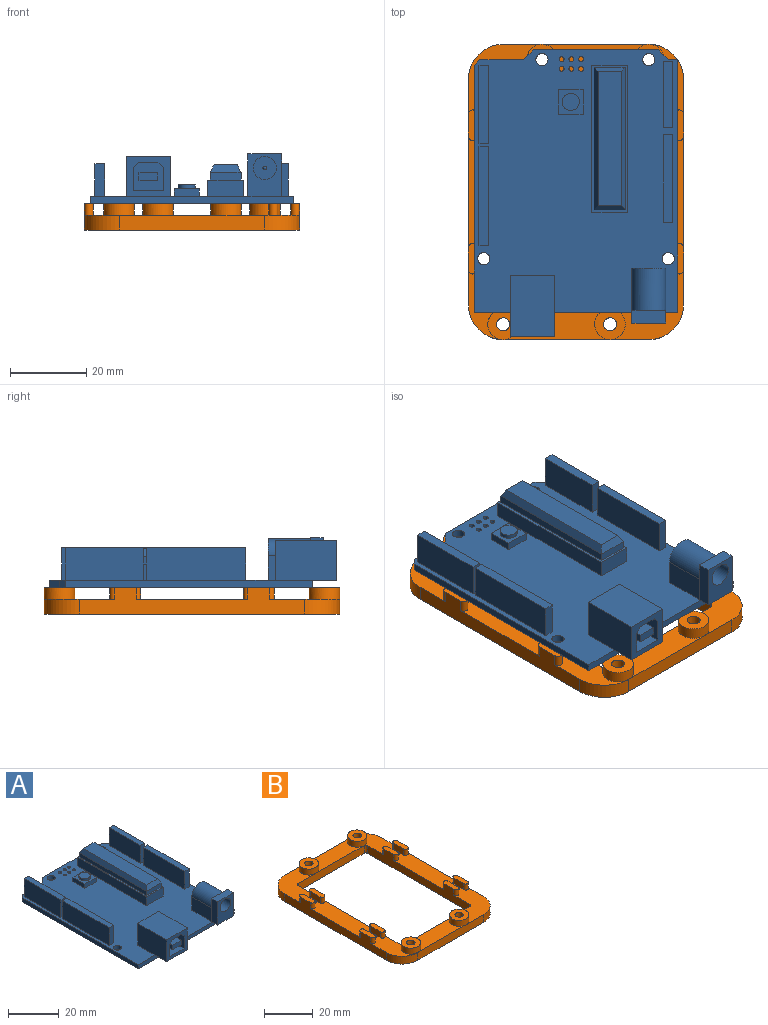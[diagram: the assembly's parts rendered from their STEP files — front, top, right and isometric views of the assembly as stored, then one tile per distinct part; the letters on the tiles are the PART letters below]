
ASSEMBLY  parts=2 mates=1
PART A: 159 faces, bbox 53.3x75x13 mm
  f0: plane 68.58x53.34mm, normal (0,0,1), area 2744.3mm2, adj f1,f2,f3,f4,f5,f6,f7,f8
  f1: plane 2.54x2.54mm, normal (0.71,0.71,0), area 6.8mm2, adj f0,f2,f51,f52
  f2: plane 32.77x1.9mm, normal (0,1,0), area 62.3mm2, adj f0,f1,f3,f52
  f3: plane 2.54x2.54mm, normal (-0.71,0.71,0), area 6.8mm2, adj f0,f2,f4,f52
  f4: plane 11.43x1.9mm, normal (0,1,0), area 21.7mm2, adj f0,f3,f5,f52
  f5: plane 1.9x1.52mm, normal (-0.71,0.71,0), area 4.1mm2, adj f0,f4,f6,f52
  f6: plane 64.52x1.9mm, normal (-1,0,0), area 122.6mm2, adj f0,f5,f7,f52
  f7: plane 53.34x1.9mm, normal (0,-1,0), area 101.3mm2, adj f0,f6,f8,f52,f81,f99,f107,f108
  f8: plane 66.04x1.9mm, normal (1,0,0), area 125.5mm2, adj f0,f7,f51,f52
  f9: cylinder r=1.59mm len=3.18mm, axis (0,0,-1), area 19mm2, adj f0,f52
  f10: cylinder r=1.59mm len=3.18mm, axis (0,0,-1), area 19mm2, adj f0,f52
  f11: cylinder r=1.59mm len=3.18mm, axis (0,0,-1), area 19mm2, adj f0,f52
  f12: cylinder r=1.59mm len=3.18mm, axis (0,0,-1), area 19mm2, adj f0,f52
  f13: cylinder r=0.64mm len=1.9mm, axis (0,0,-1), area 7.6mm2, adj f52,f80
  f14: cylinder r=0.64mm len=1.9mm, axis (0,0,-1), area 7.6mm2, adj f52,f79
  f15: cylinder r=0.64mm len=1.9mm, axis (0,0,-1), area 7.6mm2, adj f52,f78
  f16: cylinder r=0.64mm len=1.9mm, axis (0,0,-1), area 7.6mm2, adj f52,f77
  f17: cylinder r=0.64mm len=1.9mm, axis (0,0,-1), area 7.6mm2, adj f52,f76
  f18: cylinder r=0.64mm len=1.9mm, axis (0,0,-1), area 7.6mm2, adj f52,f75
  f19: cylinder r=0.64mm len=1.9mm, axis (0,0,-1), area 7.6mm2, adj f52,f74
  f20: cylinder r=0.64mm len=1.9mm, axis (0,0,-1), area 7.6mm2, adj f52,f73
  f21: cylinder r=0.64mm len=1.9mm, axis (0,0,-1), area 7.6mm2, adj f52,f72
  f22: cylinder r=0.64mm len=1.9mm, axis (0,0,-1), area 7.6mm2, adj f52,f71
  f23: cylinder r=0.64mm len=1.9mm, axis (0,0,-1), area 7.6mm2, adj f52,f58
  f24: cylinder r=0.64mm len=1.9mm, axis (0,0,-1), area 7.6mm2, adj f52,f140
  f25: cylinder r=0.64mm len=1.9mm, axis (0,0,-1), area 7.6mm2, adj f52,f151
  f26: cylinder r=0.64mm len=1.9mm, axis (0,0,-1), area 7.6mm2, adj f52,f59
  f27: cylinder r=0.64mm len=1.9mm, axis (0,0,-1), area 7.6mm2, adj f52,f60
  f28: cylinder r=0.64mm len=1.9mm, axis (0,0,-1), area 7.6mm2, adj f52,f61
  f29: cylinder r=0.64mm len=1.9mm, axis (0,0,-1), area 7.6mm2, adj f52,f62
  f30: cylinder r=0.64mm len=1.9mm, axis (0,0,-1), area 7.6mm2, adj f52,f63
  f31: cylinder r=0.64mm len=1.9mm, axis (0,0,-1), area 7.6mm2, adj f52,f64
  f32: cylinder r=0.64mm len=1.9mm, axis (0,0,-1), area 7.6mm2, adj f52,f65
  f33: cylinder r=0.64mm len=1.9mm, axis (0,0,-1), area 7.6mm2, adj f52,f139
  f34: cylinder r=0.64mm len=1.9mm, axis (0,0,-1), area 7.6mm2, adj f52,f138
  f35: cylinder r=0.64mm len=1.9mm, axis (0,0,-1), area 7.6mm2, adj f52,f137
  f36: cylinder r=0.64mm len=1.9mm, axis (0,0,-1), area 7.6mm2, adj f52,f136
  f37: cylinder r=0.64mm len=1.9mm, axis (0,0,-1), area 7.6mm2, adj f52,f135
  f38: cylinder r=0.64mm len=1.9mm, axis (0,0,-1), area 7.6mm2, adj f52,f134
  f39: cylinder r=0.64mm len=1.9mm, axis (0,0,-1), area 7.6mm2, adj f52,f133
  f40: cylinder r=0.64mm len=1.9mm, axis (0,0,-1), area 7.6mm2, adj f52,f150
  f41: cylinder r=0.64mm len=1.9mm, axis (0,0,-1), area 7.6mm2, adj f52,f149
  f42: cylinder r=0.64mm len=1.9mm, axis (0,0,-1), area 7.6mm2, adj f52,f148
  f43: cylinder r=0.64mm len=1.9mm, axis (0,0,-1), area 7.6mm2, adj f52,f147
  f44: cylinder r=0.64mm len=1.9mm, axis (0,0,-1), area 7.6mm2, adj f52,f146
  f45: cylinder r=0.64mm len=1.9mm, axis (0,0,-1), area 7.6mm2, adj f0,f52
  f46: cylinder r=0.64mm len=1.9mm, axis (0,0,-1), area 7.6mm2, adj f0,f52
  f47: cylinder r=0.64mm len=1.9mm, axis (0,0,-1), area 7.6mm2, adj f0,f52
  f48: cylinder r=0.64mm len=1.9mm, axis (0,0,-1), area 7.6mm2, adj f0,f52
  f49: cylinder r=0.64mm len=1.9mm, axis (0,0,-1), area 7.6mm2, adj f0,f52
  f50: cylinder r=0.64mm len=1.9mm, axis (0,0,-1), area 7.6mm2, adj f0,f52
  f51: plane 2.54x1.9mm, normal (0,1,0), area 4.8mm2, adj f0,f1,f8,f52
  f52: plane 68.58x53.34mm, normal (0,0,-1), area 3531.3mm2, adj f1,f2,f3,f4,f5,f6,f7,f8
  f53: plane 20.48x2.5mm, normal (0,0,1), area 51.2mm2, adj f54,f55,f56,f57
  f54: plane 8.6x2.5mm, normal (0,1,0), area 21.5mm2, adj f0,f53,f55,f57
  f55: plane 20.48x8.6mm, normal (1,0,0), area 176.1mm2, adj f0,f53,f54,f56
  f56: plane 8.6x2.5mm, normal (0,-1,0), area 21.5mm2, adj f0,f53,f55,f57
  f57: plane 20.48x8.6mm, normal (-1,0,0), area 176.1mm2, adj f0,f53,f54,f56
  f58: plane 1.27x1.27mm, normal (0,0,-1), area 1.3mm2, adj f23
  f59: plane 1.27x1.27mm, normal (0,0,-1), area 1.3mm2, adj f26
  f60: plane 1.27x1.27mm, normal (0,0,-1), area 1.3mm2, adj f27
  f61: plane 1.27x1.27mm, normal (0,0,-1), area 1.3mm2, adj f28
  f62: plane 1.27x1.27mm, normal (0,0,-1), area 1.3mm2, adj f29
  f63: plane 1.27x1.27mm, normal (0,0,-1), area 1.3mm2, adj f30
  f64: plane 1.27x1.27mm, normal (0,0,-1), area 1.3mm2, adj f31
  f65: plane 1.27x1.27mm, normal (0,0,-1), area 1.3mm2, adj f32
  f66: plane 26x2.5mm, normal (0,0,1), area 65mm2, adj f67,f68,f69,f70
  f67: plane 26x8.6mm, normal (1,0,0), area 223.6mm2, adj f0,f66,f68,f70
  f68: plane 8.6x2.5mm, normal (0,-1,0), area 21.5mm2, adj f0,f66,f67,f69
  f69: plane 26x8.6mm, normal (-1,0,0), area 223.6mm2, adj f0,f66,f68,f70
  f70: plane 8.6x2.5mm, normal (0,1,0), area 21.5mm2, adj f0,f66,f67,f69
  f71: plane 1.27x1.27mm, normal (0,0,-1), area 1.3mm2, adj f22
  f72: plane 1.27x1.27mm, normal (0,0,-1), area 1.3mm2, adj f21
  f73: plane 1.27x1.27mm, normal (0,0,-1), area 1.3mm2, adj f20
  f74: plane 1.27x1.27mm, normal (0,0,-1), area 1.3mm2, adj f19
  f75: plane 1.27x1.27mm, normal (0,0,-1), area 1.3mm2, adj f18
  f76: plane 1.27x1.27mm, normal (0,0,-1), area 1.3mm2, adj f17
  f77: plane 1.27x1.27mm, normal (0,0,-1), area 1.3mm2, adj f16
  f78: plane 1.27x1.27mm, normal (0,0,-1), area 1.3mm2, adj f15
  f79: plane 1.27x1.27mm, normal (0,0,-1), area 1.3mm2, adj f14
  f80: plane 1.27x1.27mm, normal (0,0,-1), area 1.3mm2, adj f13
  f81: plane 11.6x6.38mm, normal (0,0,-1), area 73.9mm2, adj f7,f82,f83,f85
  f82: plane 11.6x10.5mm, normal (0,-1,0), area 64.6mm2, adj f81,f83,f85,f86,f87,f88,f89,f90
  f83: plane 16x10.5mm, normal (1,0,0), area 168mm2, adj f0,f81,f82,f84,f86
  f84: plane 11.6x10.5mm, normal (0,1,0), area 121.8mm2, adj f0,f83,f85,f86
  f85: plane 16x10.5mm, normal (-1,0,0), area 168mm2, adj f0,f81,f82,f84,f86
  f86: plane 16x11.6mm, normal (0,0,1), area 185.6mm2, adj f82,f83,f84,f85
  f87: plane 14.14x5.02mm, normal (0,0,-1), area 71mm2, adj f82,f88,f92,f93
  f88: plane 14.14x1.44mm, normal (0.71,0,-0.71), area 28.8mm2, adj f82,f87,f89,f93
  f89: plane 14.14x6.06mm, normal (1,0,0), area 85.7mm2, adj f82,f88,f90,f93
  f90: plane 14.14x7.9mm, normal (0,0,1), area 111.7mm2, adj f82,f89,f91,f93
  f91: plane 14.14x6.06mm, normal (-1,0,0), area 85.7mm2, adj f82,f90,f92,f93
  f92: plane 14.14x1.44mm, normal (-0.71,0,-0.71), area 28.8mm2, adj f82,f87,f91,f93
  f93: plane 7.9x7.5mm, normal (0,-1,0), area 47mm2, adj f87,f88,f89,f90,f91,f92,f95,f96
  f94: plane 4.88x2.08mm, normal (0,-1,0), area 10.2mm2, adj f95,f96,f97,f98
  f95: plane 14.14x4.88mm, normal (0,0,1), area 69mm2, adj f93,f94,f96,f98
  f96: plane 14.14x2.08mm, normal (-1,0,0), area 29.4mm2, adj f93,f94,f95,f97
  f97: plane 14.14x4.88mm, normal (0,0,-1), area 69mm2, adj f93,f94,f96,f98
  f98: plane 14.14x2.08mm, normal (1,0,0), area 29.4mm2, adj f93,f94,f95,f97
  f99: plane 8.88x2.88mm, normal (0,0,-1), area 25.5mm2, adj f7,f107,f108,f109
  f100: plane 11x6.49mm, normal (1,0,0), area 71.4mm2, adj f0,f101,f103,f104
  f101: cylinder r=4.44mm len=11mm, axis (0,-1,0), area 153.4mm2, adj f100,f102,f103,f104,f105
  f102: plane 11x6.49mm, normal (-1,0,0), area 71.4mm2, adj f0,f101,f103,f105
  f103: plane 10.93x8.88mm, normal (0,1,0), area 88.6mm2, adj f0,f100,f101,f102
  f104: plane 6.63x0mm, normal (0,-1,0), area 0mm2, adj f0,f100,f101,f108
  f105: plane 11.12x8.88mm, normal (0,1,0), area 10.1mm2, adj f0,f101,f102,f106,f107,f108
  f106: plane 8.88x3.3mm, normal (0,0,1), area 29.3mm2, adj f105,f107,f108,f109
  f107: plane 11.13x3.3mm, normal (-1,0,0), area 36.7mm2, adj f0,f7,f99,f105,f106,f109
  f108: plane 11.13x3.3mm, normal (1,0,0), area 36.7mm2, adj f0,f7,f99,f104,f105,f106,f109
  f109: plane 11.13x8.88mm, normal (0,-1,0), area 70.5mm2, adj f99,f106,f107,f108,f110
  f110: cylinder r=3mm len=12.8mm, axis (0,-1,0), area 241.3mm2, adj f109,f111
  f111: plane 6x6mm, normal (0,-1,0), area 27.5mm2, adj f110,f112
  f112: cylinder r=0.5mm len=10mm, axis (0,1,0), area 31.4mm2, adj f111,f113
  f113: sphere r=0.5mm, area 1.6mm2, adj f112
  f114: plane 9.33x4.3mm, normal (0,-1,0), area 40.1mm2, adj f0,f115,f117,f118
  f115: plane 38.37x4.3mm, normal (1,0,0), area 164.8mm2, adj f0,f114,f116,f118
  f116: plane 9.33x4.3mm, normal (0,1,0), area 40.1mm2, adj f0,f115,f117,f118
  f117: plane 38.37x4.3mm, normal (-1,0,0), area 164.8mm2, adj f0,f114,f116,f118
  f118: plane 38.37x9.33mm, normal (0,0,1), area 57.4mm2, adj f114,f115,f116,f117,f119,f120,f121,f122
  f119: plane 37.19x2mm, normal (-1,0,0), area 74.4mm2, adj f118,f120,f122,f127
  f120: plane 8.08x2mm, normal (0,-1,0), area 16.2mm2, adj f118,f119,f121,f126
  f121: plane 37.19x2mm, normal (1,0,0), area 74.4mm2, adj f118,f120,f122,f125
  f122: plane 8.08x2mm, normal (0,1,0), area 16.2mm2, adj f118,f119,f121,f124
  f123: plane 35.16x6.05mm, normal (0,0,1), area 212.7mm2, adj f124,f125,f126,f127
  f124: plane 8.08x2mm, normal (0,0.9,0.44), area 15.7mm2, adj f122,f123,f125,f127
  f125: plane 37.19x2mm, normal (0.89,0,0.45), area 81.1mm2, adj f121,f123,f124,f126
  f126: plane 8.08x2mm, normal (0,-0.88,0.47), area 16mm2, adj f120,f123,f125,f127
  f127: plane 37.19x2mm, normal (-0.89,0,0.45), area 81.2mm2, adj f119,f123,f124,f126
  f128: plane 23x2.44mm, normal (0,0,1), area 56mm2, adj f129,f130,f131,f132
  f129: plane 23x8.6mm, normal (1,0,0), area 197.8mm2, adj f0,f128,f130,f132
  f130: plane 8.6x2.44mm, normal (0,-1,0), area 20.9mm2, adj f0,f128,f129,f131
  f131: plane 23x8.6mm, normal (-1,0,0), area 197.8mm2, adj f0,f128,f130,f132
  f132: plane 8.6x2.44mm, normal (0,1,0), area 20.9mm2, adj f0,f128,f129,f131
  f133: plane 1.27x1.27mm, normal (0,0,-1), area 1.3mm2, adj f39
  f134: plane 1.27x1.27mm, normal (0,0,-1), area 1.3mm2, adj f38
  f135: plane 1.27x1.27mm, normal (0,0,-1), area 1.3mm2, adj f37
  f136: plane 1.27x1.27mm, normal (0,0,-1), area 1.3mm2, adj f36
  f137: plane 1.27x1.27mm, normal (0,0,-1), area 1.3mm2, adj f35
  f138: plane 1.27x1.27mm, normal (0,0,-1), area 1.3mm2, adj f34
  f139: plane 1.27x1.27mm, normal (0,0,-1), area 1.3mm2, adj f33
  f140: plane 1.27x1.27mm, normal (0,0,-1), area 1.3mm2, adj f24
  f141: plane 17.27x2.44mm, normal (0,0,1), area 42.1mm2, adj f142,f143,f144,f145
  f142: plane 8.6x2.44mm, normal (0,-1,0), area 20.9mm2, adj f0,f141,f143,f145
  f143: plane 17.27x8.6mm, normal (-1,0,0), area 148.6mm2, adj f0,f141,f142,f144
  f144: plane 8.6x2.44mm, normal (0,1,0), area 20.9mm2, adj f0,f141,f143,f145
  f145: plane 17.27x8.6mm, normal (1,0,0), area 148.6mm2, adj f0,f141,f142,f144
  f146: plane 1.27x1.27mm, normal (0,0,-1), area 1.3mm2, adj f44
  f147: plane 1.27x1.27mm, normal (0,0,-1), area 1.3mm2, adj f43
  f148: plane 1.27x1.27mm, normal (0,0,-1), area 1.3mm2, adj f42
  f149: plane 1.27x1.27mm, normal (0,0,-1), area 1.3mm2, adj f41
  f150: plane 1.27x1.27mm, normal (0,0,-1), area 1.3mm2, adj f40
  f151: plane 1.27x1.27mm, normal (0,0,-1), area 1.3mm2, adj f25
  f152: plane 6.5x2mm, normal (-1,0,0), area 13mm2, adj f0,f153,f155,f156
  f153: plane 6.5x2mm, normal (0,-1,0), area 13mm2, adj f0,f152,f154,f156
  f154: plane 6.5x2mm, normal (1,0,0), area 13mm2, adj f0,f153,f155,f156
  f155: plane 6.5x2mm, normal (0,1,0), area 13mm2, adj f0,f152,f154,f156
  f156: plane 6.5x6.5mm, normal (0,0,1), area 26.4mm2, adj f152,f153,f154,f155,f157
  f157: cylinder r=2.24mm len=4.49mm, axis (0,0,-1), area 14.1mm2, adj f156,f158
  f158: plane 4.49x4.49mm, normal (0,0,1), area 15.8mm2, adj f157
PART B: 129 faces, bbox 56.3x77.2x6.9 mm
  f0: cylinder r=1.7mm len=4.2mm, axis (0,0,1), area 44.9mm2, adj f36,f107
  f1: cylinder r=1.7mm len=3.4mm, axis (0,0,1), area 12.8mm2, adj f9,f11,f100
  f2: cylinder r=1.7mm len=3.4mm, axis (0,0,1), area 12.8mm2, adj f9,f10,f93
  f3: cylinder r=1.7mm len=4.2mm, axis (0,0,1), area 44.9mm2, adj f38,f86
  f4: cylinder r=1.7mm len=4.2mm, axis (0,0,1), area 44.9mm2, adj f40,f79
  f5: cylinder r=1.7mm len=3.4mm, axis (0,0,1), area 12.8mm2, adj f12,f14,f128
  f6: cylinder r=1.7mm len=3.4mm, axis (0,0,1), area 12.8mm2, adj f12,f13,f121
  f7: cylinder r=1.7mm len=4.2mm, axis (0,0,1), area 44.9mm2, adj f34,f114
  f8: plane 77.23x56.26mm, normal (0,0,-1), area 1560.6mm2, adj f17,f18,f19,f20,f21,f22,f23,f24
  f9: plane 34.91x8mm, normal (0,0,1), area 235.7mm2, adj f1,f2,f22,f29,f54,f55,f57,f58
  f10: plane 21.16x19.24mm, normal (0,0,1), area 194.8mm2, adj f2,f22,f23,f27,f28,f29,f31,f37
  f11: plane 21.16x9.08mm, normal (0,0,1), area 113.5mm2, adj f1,f21,f22,f29,f30,f35,f53,f54
  f12: plane 34.91x8mm, normal (0,0,1), area 235.7mm2, adj f5,f6,f18,f25,f41,f43,f45,f46
  f13: plane 21.16x19.24mm, normal (0,0,1), area 194.8mm2, adj f6,f18,f19,f20,f24,f25,f32,f33
  f14: plane 21.16x9.08mm, normal (0,0,1), area 113.5mm2, adj f5,f17,f18,f25,f26,f39,f41,f42
  f15: plane 27.94x8mm, normal (0,0,1), area 173.3mm2, adj f27,f31,f37,f39
  f16: plane 27.94x8mm, normal (0,0,1), area 173.3mm2, adj f20,f32,f33,f35
  f17: cylinder r=1.08mm len=3.9mm, axis (0,0,1), area 6.6mm2, adj f8,f14,f18,f31
  f18: plane 59.07x6.9mm, normal (1,0,0), area 264.6mm2, adj f8,f12,f13,f14,f17,f19,f42,f43
  f19: cylinder r=1.08mm len=3.9mm, axis (0,0,1), area 6.6mm2, adj f8,f13,f18,f20
  f20: plane 38.1x3.9mm, normal (0,-1,0), area 148.6mm2, adj f8,f13,f16,f19,f21
  f21: cylinder r=1.08mm len=3.9mm, axis (0,0,1), area 6.6mm2, adj f8,f11,f20,f22
  f22: plane 59.07x6.9mm, normal (-1,0,0), area 264.6mm2, adj f8,f9,f10,f11,f21,f23,f65,f66
  f23: cylinder r=1.08mm len=3.9mm, axis (0,0,1), area 6.6mm2, adj f8,f10,f22,f31
  f24: cylinder r=9.08mm len=9.08mm, axis (0,0,1), area 55.6mm2, adj f8,f13,f25,f32
  f25: plane 59.07x6.9mm, normal (-1,0,0), area 264.6mm2, adj f8,f12,f13,f14,f24,f26,f46,f47
  f26: cylinder r=9.08mm len=9.08mm, axis (0,0,1), area 55.6mm2, adj f8,f14,f25,f27
  f27: plane 38.1x3.9mm, normal (0,-1,0), area 148.6mm2, adj f8,f10,f15,f26,f28
  f28: cylinder r=9.08mm len=9.08mm, axis (0,0,1), area 55.6mm2, adj f8,f10,f27,f29
  f29: plane 59.07x6.9mm, normal (1,0,0), area 264.6mm2, adj f8,f9,f10,f11,f28,f30,f53,f55
  f30: cylinder r=9.08mm len=9.08mm, axis (0,0,1), area 55.6mm2, adj f8,f11,f29,f32
  f31: plane 38.1x3.9mm, normal (0,1,0), area 148.6mm2, adj f8,f10,f15,f17,f23
  f32: plane 38.1x3.9mm, normal (0,1,0), area 148.6mm2, adj f8,f13,f16,f24,f30
  f33: cylinder r=4mm len=8mm, axis (0,0,-1), area 75.4mm2, adj f13,f16,f34
  f34: plane 8x8mm, normal (0,0,1), area 41.2mm2, adj f7,f33
  f35: cylinder r=4mm len=8mm, axis (0,0,-1), area 75.4mm2, adj f11,f16,f36
  f36: plane 8x8mm, normal (0,0,1), area 41.2mm2, adj f0,f35
  f37: cylinder r=4mm len=8mm, axis (0,0,-1), area 75.4mm2, adj f10,f15,f38
  f38: plane 8x8mm, normal (0,0,1), area 41.2mm2, adj f3,f37
  f39: cylinder r=4mm len=8mm, axis (0,0,-1), area 75.4mm2, adj f14,f15,f40
  f40: plane 8x8mm, normal (0,0,1), area 41.2mm2, adj f4,f39
  f41: plane 5.7x3mm, normal (-1,0,0), area 17.1mm2, adj f12,f14,f42,f43,f44
  f42: cylinder r=1.15mm len=3mm, axis (0,0,-1), area 10.8mm2, adj f14,f18,f41,f44
  f43: cylinder r=1.15mm len=3mm, axis (0,0,-1), area 10.8mm2, adj f12,f18,f41,f44
  f44: plane 8x2.3mm, normal (0,0,1), area 17.3mm2, adj f18,f41,f42,f43
  f45: plane 5.7x3mm, normal (1,0,0), area 17.1mm2, adj f12,f14,f46,f47,f48
  f46: cylinder r=1.15mm len=3mm, axis (0,0,-1), area 10.8mm2, adj f12,f25,f45,f48
  f47: cylinder r=1.15mm len=3mm, axis (0,0,-1), area 10.8mm2, adj f14,f25,f45,f48
  f48: plane 8x2.3mm, normal (0,0,1), area 17.3mm2, adj f25,f45,f46,f47
  f49: cylinder r=1.15mm len=3mm, axis (0,0,-1), area 10.8mm2, adj f13,f25,f51,f52
  f50: cylinder r=1.15mm len=3mm, axis (0,0,-1), area 10.8mm2, adj f12,f25,f51,f52
  f51: plane 5.7x3mm, normal (1,0,0), area 17.1mm2, adj f12,f13,f49,f50,f52
  f52: plane 8x2.3mm, normal (0,0,1), area 17.3mm2, adj f25,f49,f50,f51
  f53: cylinder r=1.15mm len=3mm, axis (0,0,-1), area 10.8mm2, adj f11,f29,f54,f56
  f54: plane 5.7x3mm, normal (-1,0,0), area 17.1mm2, adj f9,f11,f53,f55,f56
  f55: cylinder r=1.15mm len=3mm, axis (0,0,-1), area 10.8mm2, adj f9,f29,f54,f56
  f56: plane 8x2.3mm, normal (0,0,1), area 17.3mm2, adj f29,f53,f54,f55
  f57: cylinder r=1.15mm len=3mm, axis (0,0,-1), area 10.8mm2, adj f9,f29,f58,f60
  f58: plane 5.7x3mm, normal (-1,0,0), area 17.1mm2, adj f9,f10,f57,f59,f60
  f59: cylinder r=1.15mm len=3mm, axis (0,0,-1), area 10.8mm2, adj f10,f29,f58,f60
  f60: plane 8x2.3mm, normal (0,0,1), area 17.3mm2, adj f29,f57,f58,f59
  f61: cylinder r=1.15mm len=3mm, axis (0,0,-1), area 10.8mm2, adj f13,f18,f62,f64
  f62: plane 5.7x3mm, normal (-1,0,0), area 17.1mm2, adj f12,f13,f61,f63,f64
  f63: cylinder r=1.15mm len=3mm, axis (0,0,-1), area 10.8mm2, adj f12,f18,f62,f64
  f64: plane 8x2.3mm, normal (0,0,1), area 17.3mm2, adj f18,f61,f62,f63
  f65: cylinder r=1.15mm len=3mm, axis (0,0,-1), area 10.8mm2, adj f11,f22,f67,f68
  f66: cylinder r=1.15mm len=3mm, axis (0,0,-1), area 10.8mm2, adj f9,f22,f67,f68
  f67: plane 5.7x3mm, normal (1,0,0), area 17.1mm2, adj f9,f11,f65,f66,f68
  f68: plane 8x2.3mm, normal (0,0,1), area 17.3mm2, adj f22,f65,f66,f67
  f69: cylinder r=1.15mm len=3mm, axis (0,0,-1), area 10.8mm2, adj f9,f22,f71,f72
  f70: cylinder r=1.15mm len=3mm, axis (0,0,-1), area 10.8mm2, adj f10,f22,f71,f72
  f71: plane 5.7x3mm, normal (1,0,0), area 17.1mm2, adj f9,f10,f69,f70,f72
  f72: plane 8x2.3mm, normal (0,0,1), area 17.3mm2, adj f22,f69,f70,f71
  f73: plane 3x2.7mm, normal (-0.87,0.5,0), area 9.4mm2, adj f8,f74,f78,f79
  f74: plane 3.46x2.7mm, normal (0,1,0), area 9.4mm2, adj f8,f73,f75,f79
  f75: plane 3x2.7mm, normal (0.87,0.5,0), area 9.4mm2, adj f8,f74,f76,f79
  f76: plane 3x2.7mm, normal (0.87,-0.5,0), area 9.4mm2, adj f8,f75,f77,f79
  f77: plane 3.46x2.7mm, normal (0,-1,0), area 9.4mm2, adj f8,f76,f78,f79
  f78: plane 3x2.7mm, normal (-0.87,-0.5,0), area 9.4mm2, adj f8,f73,f77,f79
  f79: plane 6.93x6mm, normal (0,0,-1), area 22.1mm2, adj f4,f73,f74,f75,f76,f77,f78
  f80: plane 3x2.7mm, normal (-0.87,0.5,0), area 9.4mm2, adj f8,f81,f85,f86
  f81: plane 3.46x2.7mm, normal (0,1,0), area 9.4mm2, adj f8,f80,f82,f86
  f82: plane 3x2.7mm, normal (0.87,0.5,0), area 9.4mm2, adj f8,f81,f83,f86
  f83: plane 3x2.7mm, normal (0.87,-0.5,0), area 9.4mm2, adj f8,f82,f84,f86
  f84: plane 3.46x2.7mm, normal (0,-1,0), area 9.4mm2, adj f8,f83,f85,f86
  f85: plane 3x2.7mm, normal (-0.87,-0.5,0), area 9.4mm2, adj f8,f80,f84,f86
  f86: plane 6.93x6mm, normal (0,0,-1), area 22.1mm2, adj f3,f80,f81,f82,f83,f84,f85
  f87: plane 3.46x2.7mm, normal (-1,0,0), area 9.4mm2, adj f8,f88,f92,f93
  f88: plane 3x2.7mm, normal (-0.5,0.87,0), area 9.4mm2, adj f8,f87,f89,f93
  f89: plane 3x2.7mm, normal (0.5,0.87,0), area 9.4mm2, adj f8,f88,f90,f93
  f90: plane 3.46x2.7mm, normal (1,0,0), area 9.4mm2, adj f8,f89,f91,f93
  f91: plane 3x2.7mm, normal (0.5,-0.87,0), area 9.4mm2, adj f8,f90,f92,f93
  f92: plane 3x2.7mm, normal (-0.5,-0.87,0), area 9.4mm2, adj f8,f87,f91,f93
  f93: plane 6.93x6mm, normal (0,0,-1), area 22.1mm2, adj f2,f87,f88,f89,f90,f91,f92
  f94: plane 3.46x2.7mm, normal (-1,0,0), area 9.4mm2, adj f8,f95,f99,f100
  f95: plane 3x2.7mm, normal (-0.5,0.87,0), area 9.4mm2, adj f8,f94,f96,f100
  f96: plane 3x2.7mm, normal (0.5,0.87,0), area 9.4mm2, adj f8,f95,f97,f100
  f97: plane 3.46x2.7mm, normal (1,0,0), area 9.4mm2, adj f8,f96,f98,f100
  f98: plane 3x2.7mm, normal (0.5,-0.87,0), area 9.4mm2, adj f8,f97,f99,f100
  f99: plane 3x2.7mm, normal (-0.5,-0.87,0), area 9.4mm2, adj f8,f94,f98,f100
  f100: plane 6.93x6mm, normal (0,0,-1), area 22.1mm2, adj f1,f94,f95,f96,f97,f98,f99
  f101: plane 3x2.7mm, normal (-0.87,0.5,0), area 9.4mm2, adj f8,f102,f106,f107
  f102: plane 3.46x2.7mm, normal (0,1,0), area 9.4mm2, adj f8,f101,f103,f107
  f103: plane 3x2.7mm, normal (0.87,0.5,0), area 9.4mm2, adj f8,f102,f104,f107
  f104: plane 3x2.7mm, normal (0.87,-0.5,0), area 9.4mm2, adj f8,f103,f105,f107
  f105: plane 3.46x2.7mm, normal (0,-1,0), area 9.4mm2, adj f8,f104,f106,f107
  f106: plane 3x2.7mm, normal (-0.87,-0.5,0), area 9.4mm2, adj f8,f101,f105,f107
  f107: plane 6.93x6mm, normal (0,0,-1), area 22.1mm2, adj f0,f101,f102,f103,f104,f105,f106
  f108: plane 3x2.7mm, normal (-0.87,0.5,0), area 9.4mm2, adj f8,f109,f113,f114
  f109: plane 3.46x2.7mm, normal (0,1,0), area 9.4mm2, adj f8,f108,f110,f114
  f110: plane 3x2.7mm, normal (0.87,0.5,0), area 9.4mm2, adj f8,f109,f111,f114
  f111: plane 3x2.7mm, normal (0.87,-0.5,0), area 9.4mm2, adj f8,f110,f112,f114
  f112: plane 3.46x2.7mm, normal (0,-1,0), area 9.4mm2, adj f8,f111,f113,f114
  f113: plane 3x2.7mm, normal (-0.87,-0.5,0), area 9.4mm2, adj f8,f108,f112,f114
  f114: plane 6.93x6mm, normal (0,0,-1), area 22.1mm2, adj f7,f108,f109,f110,f111,f112,f113
  f115: plane 3.46x2.7mm, normal (-1,0,0), area 9.4mm2, adj f8,f116,f120,f121
  f116: plane 3x2.7mm, normal (-0.5,0.87,0), area 9.4mm2, adj f8,f115,f117,f121
  f117: plane 3x2.7mm, normal (0.5,0.87,0), area 9.4mm2, adj f8,f116,f118,f121
  f118: plane 3.46x2.7mm, normal (1,0,0), area 9.4mm2, adj f8,f117,f119,f121
  f119: plane 3x2.7mm, normal (0.5,-0.87,0), area 9.4mm2, adj f8,f118,f120,f121
  f120: plane 3x2.7mm, normal (-0.5,-0.87,0), area 9.4mm2, adj f8,f115,f119,f121
  f121: plane 6.93x6mm, normal (0,0,-1), area 22.1mm2, adj f6,f115,f116,f117,f118,f119,f120
  f122: plane 3.46x2.7mm, normal (-1,0,0), area 9.4mm2, adj f8,f123,f127,f128
  f123: plane 3x2.7mm, normal (-0.5,0.87,0), area 9.4mm2, adj f8,f122,f124,f128
  f124: plane 3x2.7mm, normal (0.5,0.87,0), area 9.4mm2, adj f8,f123,f125,f128
  f125: plane 3.46x2.7mm, normal (1,0,0), area 9.4mm2, adj f8,f124,f126,f128
  f126: plane 3x2.7mm, normal (0.5,-0.87,0), area 9.4mm2, adj f8,f125,f127,f128
  f127: plane 3x2.7mm, normal (-0.5,-0.87,0), area 9.4mm2, adj f8,f122,f126,f128
  f128: plane 6.93x6mm, normal (0,0,-1), area 22.1mm2, adj f5,f122,f123,f124,f125,f126,f127
PLACE A t=(0,1.59,6.9)mm
PLACE B t=(0,0,3.9)mm
MATE fastened A.f9 <-> B.f7  axis (0,0,-1) through (-8.89,34.61,6.9)mm
